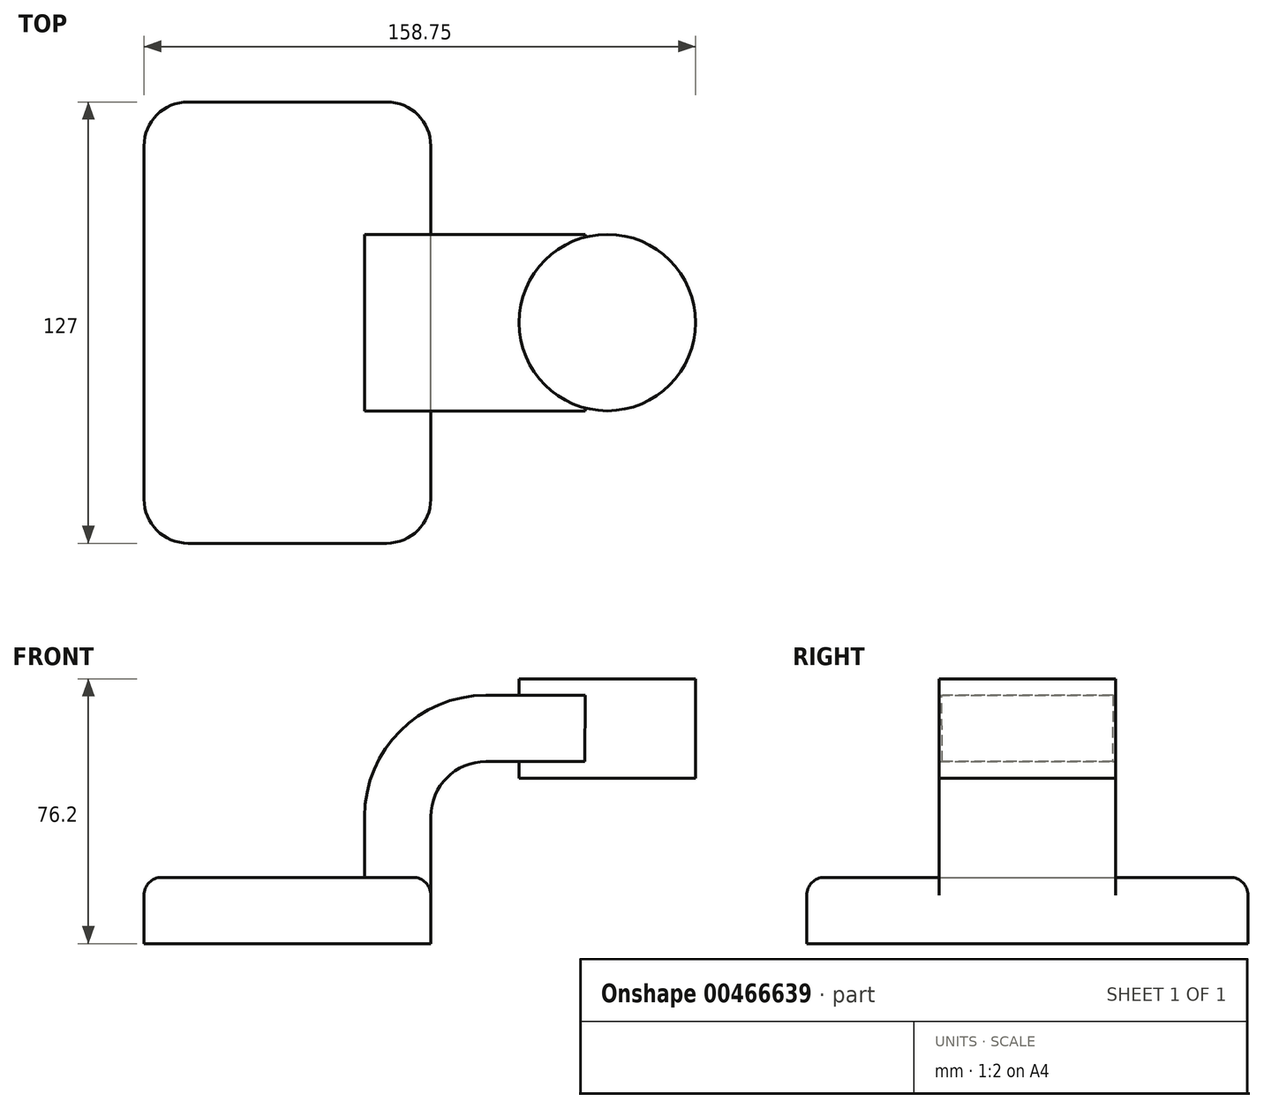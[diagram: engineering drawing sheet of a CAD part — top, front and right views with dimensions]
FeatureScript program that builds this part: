
annotation { "Feature Type Name" : "Feature", "Feature Type Description" : "" }
export const myFeature = defineFeature(function(context is Context, id is Id, definition is map)
    precondition{}
    {
        {
            var Q0;
            Q0=qCreatedBy(makeId("Front.planeOp"),FACE);
            var sketch = newSketch(context, id + "F0", { "sketchPlane" : qUnion([Q0])});
            skLineSegment(sketch, "E0.bottom", {"start": v(-48.62, 65.67) * mm, "end": v(-131.17, 65.67) * mm});
            skLineSegment(sketch, "E0.top", {"start": v(-48.62, 84.72) * mm, "end": v(-131.17, 84.72) * mm});
            skLineSegment(sketch, "E0.left", {"start": v(-48.62, 65.67) * mm, "end": v(-48.62, 84.72) * mm});
            skLineSegment(sketch, "E0.right", {"start": v(-131.17, 65.67) * mm, "end": v(-131.17, 84.72) * mm});
            skPoint(sketch, "E0.middle", {"position": v(-89.9, 75.2) * mm});
            skLineSegment(sketch, "E1.bottom", {"start": v(27.58, 113.3) * mm, "end": v(-23.22, 113.3) * mm});
            skLineSegment(sketch, "E1.top", {"start": v(27.58, 141.87) * mm, "end": v(-23.22, 141.87) * mm});
            skLineSegment(sketch, "E1.left", {"start": v(27.58, 113.3) * mm, "end": v(27.58, 141.87) * mm});
            skLineSegment(sketch, "E1.right", {"start": v(-23.22, 113.3) * mm, "end": v(-23.22, 141.87) * mm});
            skPoint(sketch, "E1.middle", {"position": v(2.18, 127.58) * mm});
            skLineSegment(sketch, "E2", {"start": v(-48.62, 84.72) * mm, "end": v(-48.62, 102.2) * mm});
            skArc(sketch, "E3", {"start": v(-48.62, 102.2) * mm, "mid": v(-43.97, 113.42) * mm, "end": v(-32.75, 118.07) * mm});
            skLineSegment(sketch, "E4", {"start": v(-32.75, 118.07) * mm, "end": v(-4.17, 118.07) * mm});
            skLineSegment(sketch, "E5.0", {"start": v(-32.75, 137.12) * mm, "end": v(-4.17, 137.12) * mm});
            skArc(sketch, "E5.1", {"start": v(-67.67, 102.2) * mm, "mid": v(-57.44, 126.89) * mm, "end": v(-32.75, 137.12) * mm});
            skLineSegment(sketch, "E5.2", {"start": v(-67.67, 84.72) * mm, "end": v(-67.67, 102.2) * mm});
            skLineSegment(sketch, "E6", {"start": v(-4.37, 113.3) * mm, "end": v(-4.17, 137.12) * mm});
            skLineSegment(sketch, "E7", {"start": v(-4.17, 137.12) * mm, "end": v(-4.17, 141.87) * mm});
            skFitSpline(sketch, "E8", {"points": [v(-131.17, 84.72) * mm, v(-32.75, 137.12) * mm], "startDerivative": vector(-0.4, 119.76) * mm, "endDerivative": vector(119.34, -0.05) * mm});
            skLineSegment(sketch, "E9", {"start": v(2.18, 127.58) * mm, "end": v(2.18, 141.87) * mm});
            skLineSegment(sketch, "E10", {"start": v(2.18, 141.87) * mm, "end": v(2.18, 113.3) * mm});
            skSolve(sketch);
        }
        {
            var Q0;
            Q0=makeQuery(id+"F0.imprint","IMPRINT",FACE,{"disambiguationData":[TD([[makeQuery(id+"F0.imprint","IMPRINT",EDGE,{"derivedFrom":sQuery(id+"F0.wireOp",EDGE,"E0.bottom")}),-1.0]])]});
            extrude(context, id + "F1", {"entities" : qUnion([Q0]), "endBound" : BoundingType.SYMMETRIC, "depth" : 127 * mm});
        }
        {
            var Q0;
            {var subQ1=sQuery(id+"F0.wireOp",EDGE,"E2");Q0=makeQuery(id+"F0.imprint","IMPRINT",FACE,{"disambiguationData":[TD([[makeQuery(id+"F0.imprint","IMPRINT",EDGE,{"derivedFrom":subQ1}),1.0]])]});}
            var Q1;
            {var subQ0=sQuery(id+"F0.wireOp",EDGE,"E4");var subQ1=sQuery(id+"F0.wireOp",EDGE,"E1.right");var subQ2=makeQuery(id+"F0.imprint","INTERSECT",VERTEX,{"derivedFrom":[subQ1,subQ0]});Q1=makeQuery(id+"F0.imprint","IMPRINT",FACE,{"disambiguationData":[TD([[makeQuery(id+"F0.imprint","IMPRINT",EDGE,{"disambiguationData":[TD([[subQ2,-1.0]])],"derivedFrom":subQ1}),-1.0]])]});}
            extrude(context, id + "F2", {"entities" : qUnion([Q0, Q1]), "operationType" : NewBodyOperationType.ADD, "endBound" : BoundingType.SYMMETRIC, "depth" : 50.8 * mm});
        }
        {
            var Q0;
            Q0=makeQuery(id+"F0.imprint","IMPRINT",FACE,{"disambiguationData":[TD([[makeQuery(id+"F0.imprint","IMPRINT",EDGE,{"derivedFrom":sQuery(id+"F0.wireOp",EDGE,"E5.1")}),1.0]])]});
            extrude(context, id + "F3", {"entities" : qUnion([Q0]), "operationType" : NewBodyOperationType.ADD, "endBound" : BoundingType.SYMMETRIC, "depth" : 15.88 * mm});
        }
        {
            var Q0;
            {var subQ4=sQuery(id+"F0.wireOp",EDGE,"E1.left");Q0=makeQuery(id+"F0.imprint","IMPRINT",FACE,{"disambiguationData":[TD([[makeQuery(id+"F0.imprint","IMPRINT",EDGE,{"derivedFrom":subQ4}),1.0]])]});}
            var Q1;
            Q1=sQuery(id+"F0.wireOp",EDGE,"E10");
            revolve(context, id + "F4", {"operationType" : NewBodyOperationType.ADD, "entities" : qUnion([Q0]), "axis" : qUnion([Q1]), "revolveType" : RevolveType.FULL});
        }
        {
            var Q0;
            Q0=makeQuery(id+"F1.opExtrude","CAP_EDGE",EDGE,{"disambiguationData":[OSD([sQuery(id+"F0.wireOp",EDGE,"E0.right")])],"isStart":false});
            var Q1;
            Q1=makeQuery(id+"F1.opExtrude","CAP_EDGE",EDGE,{"disambiguationData":[OSD([sQuery(id+"F0.wireOp",EDGE,"E0.left")])],"isStart":false});
            var Q2;
            Q2=makeQuery(id+"F1.opExtrude","CAP_EDGE",EDGE,{"disambiguationData":[OSD([sQuery(id+"F0.wireOp",EDGE,"E0.right")])],"isStart":true});
            var Q3;
            Q3=makeQuery(id+"F1.opExtrude","CAP_EDGE",EDGE,{"disambiguationData":[OSD([sQuery(id+"F0.wireOp",EDGE,"E0.left")])],"isStart":true});
            fillet(context, id + "F5", {"entities" : qUnion([Q0, Q1, Q2, Q3]), "radius" : 12.7 * mm, "tangentPropagation" : true, "allowEdgeOverflow" : false});
        }
        {
            var Q0;
            {var subQ0=sQuery(id+"F0.wireOp",EDGE,"E8");var subQ1=sQuery(id+"F0.wireOp",EDGE,"E0.top");var subQ2=sQuery(id+"F0.wireOp",EDGE,"E0.right");Q0=makeQuery(id+"F3.boolean.opBoolean","SPLIT",EDGE,{"disambiguationData":[TD([makeQuery(id+"F1.opExtrude","CAP_FACE",FACE,{"disambiguationData":[OSD([sQuery(id+"F0.wireOp",EDGE,"E0.bottom"),subQ1,sQuery(id+"F0.wireOp",EDGE,"E0.left"),subQ2])],"isStart":false})])],"derivedFrom":makeQuery(id+"F1.opExtrude","SWEPT_EDGE",EDGE,{"disambiguationData":[OSD([subQ1,subQ2,subQ0])]})});}
            var Q1;
            {var subQ0=sQuery(id+"F0.wireOp",EDGE,"E8");var subQ1=sQuery(id+"F0.wireOp",EDGE,"E0.top");var subQ2=sQuery(id+"F0.wireOp",EDGE,"E0.right");Q1=makeQuery(id+"F3.boolean.opBoolean","SPLIT",EDGE,{"disambiguationData":[TD([makeQuery(id+"F1.opExtrude","CAP_FACE",FACE,{"disambiguationData":[OSD([sQuery(id+"F0.wireOp",EDGE,"E0.bottom"),subQ1,sQuery(id+"F0.wireOp",EDGE,"E0.left"),subQ2])],"isStart":true})])],"derivedFrom":makeQuery(id+"F1.opExtrude","SWEPT_EDGE",EDGE,{"disambiguationData":[OSD([subQ1,subQ2,subQ0])]})});}
            var Q2;
            Q2=makeQuery(id+"F3.opExtrude","CAP_EDGE",EDGE,{"disambiguationData":[OSD([sQuery(id+"F0.wireOp",EDGE,"E8")])],"isStart":false});
            var Q3;
            Q3=makeQuery(id+"F3.opExtrude","CAP_EDGE",EDGE,{"disambiguationData":[OSD([sQuery(id+"F0.wireOp",EDGE,"E8")])],"isStart":true});
            fillet(context, id + "F6", {"entities" : qUnion([Q0, Q1, Q2, Q3]), "radius" : 5.08 * mm, "tangentPropagation" : true, "allowEdgeOverflow" : false});
        }
    });
